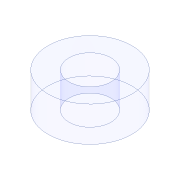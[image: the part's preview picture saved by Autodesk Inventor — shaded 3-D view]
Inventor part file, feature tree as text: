
AUTODESK INVENTOR PART (.ipt)
format: ipt  version: 2020 (Build 240168000, 168)  size: 81,920 bytes
history: native  units: mm
features: extrude x1, sketch x1
ambient origin geometry x8: Origin, YZ Plane, XZ Plane, XY Plane, X Axis, Y Axis, Z Axis, Center Point
bodies: Solid1 (feature_tree)
feature tree (2):
  extrude  "Extrusion1"  Depth=5.0mm
  sketch  "Sketch1"  dims[d0=6.0mm d1=12.0mm d2=5.0mm d3=0.0mm]
